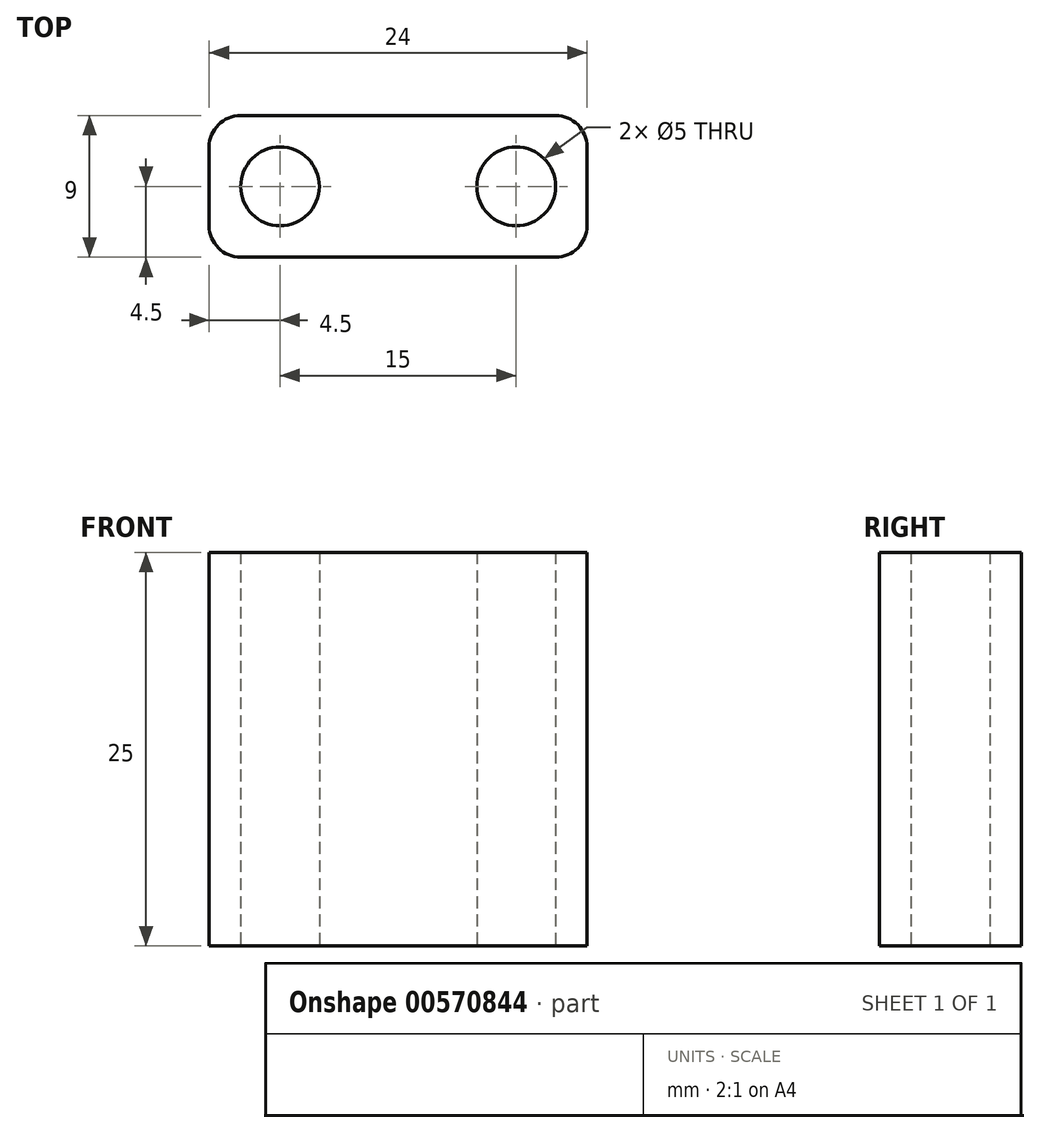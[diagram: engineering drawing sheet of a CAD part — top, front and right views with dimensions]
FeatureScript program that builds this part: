
annotation { "Feature Type Name" : "Feature", "Feature Type Description" : "" }
export const myFeature = defineFeature(function(context is Context, id is Id, definition is map)
    precondition{}
    {
        {
            var Q0;
            Q0=qCreatedBy(makeId("Top.planeOp"),FACE);
            var sketch = newSketch(context, id + "F0", { "sketchPlane" : qUnion([Q0])});
            skLineSegment(sketch, "E0.bottom", {"start": v(-12, 4.5) * mm, "end": v(12, 4.5) * mm});
            skLineSegment(sketch, "E0.top", {"start": v(-12, -4.5) * mm, "end": v(12, -4.5) * mm});
            skLineSegment(sketch, "E0.left", {"start": v(-12, 4.5) * mm, "end": v(-12, -4.5) * mm});
            skLineSegment(sketch, "E0.right", {"start": v(12, 4.5) * mm, "end": v(12, -4.5) * mm});
            skPoint(sketch, "E0.middle", {"position": v(0, 0) * mm});
            skCircle(sketch, "E1", {"center": v(-7.5, 0) * mm, "radius": 2.5 * mm});
            skCircle(sketch, "E2", {"center": v(7.5, 0) * mm, "radius": 2.5 * mm});
            skLineSegment(sketch, "E3", {"start": v(0, 4.5) * mm, "end": v(0, -4.5) * mm, "construction": true});
            skSolve(sketch);
        }
        {
            var Q0;
            Q0 = qSketchRegion(id + "F0", true);
            extrude(context, id + "F1", {"entities" : qUnion([Q0]), "depth" : 25 * mm, "offsetDistance" : 25 * mm});
        }
        {
            var Q0;
            Q0=makeQuery(id+"F1.opExtrude","SWEPT_EDGE",EDGE,{"disambiguationData":[OSD([sQuery(id+"F0.wireOp",EDGE,"E0.bottom"),sQuery(id+"F0.wireOp",EDGE,"E0.left")])]});
            var Q1;
            Q1=makeQuery(id+"F1.opExtrude","SWEPT_EDGE",EDGE,{"disambiguationData":[OSD([sQuery(id+"F0.wireOp",EDGE,"E0.bottom"),sQuery(id+"F0.wireOp",EDGE,"E0.right")])]});
            var Q2;
            Q2=makeQuery(id+"F1.opExtrude","SWEPT_EDGE",EDGE,{"disambiguationData":[OSD([sQuery(id+"F0.wireOp",EDGE,"E0.top"),sQuery(id+"F0.wireOp",EDGE,"E0.right")])]});
            var Q3;
            Q3=makeQuery(id+"F1.opExtrude","SWEPT_EDGE",EDGE,{"disambiguationData":[OSD([sQuery(id+"F0.wireOp",EDGE,"E0.top"),sQuery(id+"F0.wireOp",EDGE,"E0.left")])]});
            fillet(context, id + "F2", {"entities" : qUnion([Q0, Q1, Q2, Q3]), "radius" : 2 * mm, "tangentPropagation" : true, "allowEdgeOverflow" : false});
        }
    });
